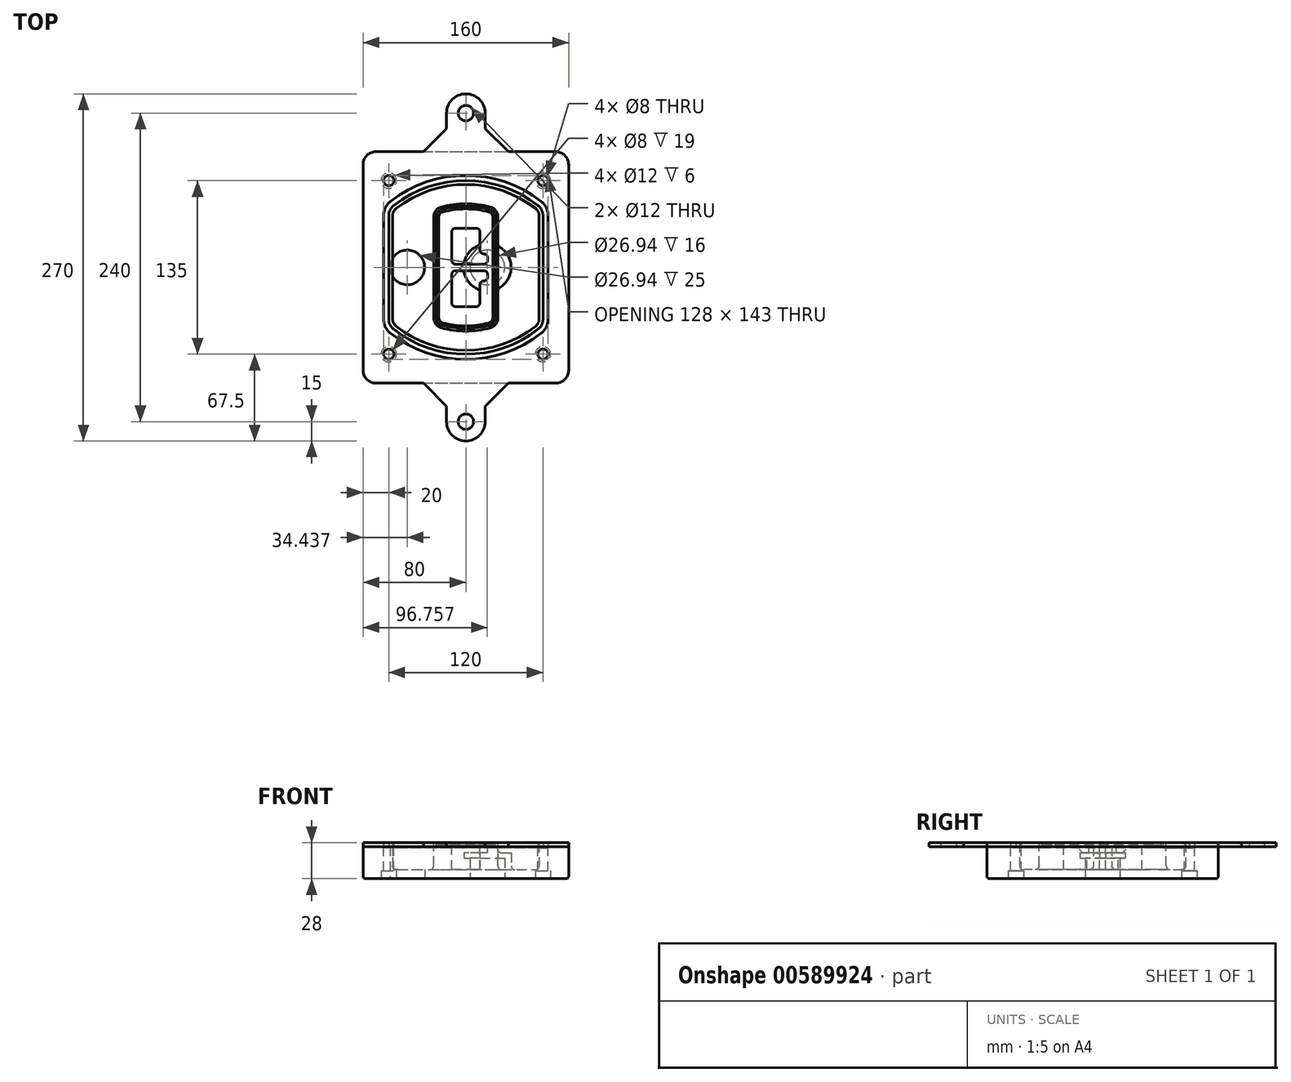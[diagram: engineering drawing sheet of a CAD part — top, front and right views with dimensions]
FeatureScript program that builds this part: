
annotation { "Feature Type Name" : "Feature", "Feature Type Description" : "" }
export const myFeature = defineFeature(function(context is Context, id is Id, definition is map)
    precondition{}
    {
        {
            var Q0;
            Q0=qCreatedBy(makeId("Top.planeOp"),FACE);
            var sketch = newSketch(context, id + "F0", { "sketchPlane" : qUnion([Q0])});
            skPoint(sketch, "E0.rect.middle", {"position": v(0, 0) * mm});
            skLineSegment(sketch, "E1.bottom", {"start": v(-70, -90) * mm, "end": v(70, -90) * mm});
            skLineSegment(sketch, "E1.top", {"start": v(-70, 90) * mm, "end": v(70, 90) * mm});
            skLineSegment(sketch, "E1.left", {"start": v(-80, -80) * mm, "end": v(-80, 80) * mm});
            skLineSegment(sketch, "E1.right", {"start": v(80, -80) * mm, "end": v(80, 80) * mm});
            skLineSegment(sketch, "E2", {"start": v(-80, 90) * mm, "end": v(80, -90) * mm, "construction": true});
            skLineSegment(sketch, "E3", {"start": v(80, 90) * mm, "end": v(-80, -90) * mm, "construction": true});
            skCircle(sketch, "E4", {"center": v(-60, 67.5) * mm, "radius": 4 * mm});
            skCircle(sketch, "E5", {"center": v(60, 67.5) * mm, "radius": 4 * mm});
            skCircle(sketch, "E6", {"center": v(60, -67.5) * mm, "radius": 4 * mm});
            skCircle(sketch, "E7", {"center": v(-60, -67.5) * mm, "radius": 4 * mm});
            skLineSegment(sketch, "E8", {"start": v(-60, 67.5) * mm, "end": v(60, 67.5) * mm, "construction": true});
            skLineSegment(sketch, "E9", {"start": v(60, 67.5) * mm, "end": v(60, -67.5) * mm, "construction": true});
            skLineSegment(sketch, "E10", {"start": v(60, -67.5) * mm, "end": v(-60, -67.5) * mm, "construction": true});
            skLineSegment(sketch, "E11", {"start": v(-60, -67.5) * mm, "end": v(-60, 67.5) * mm, "construction": true});
            skLineSegment(sketch, "E12", {"start": v(-60, 40.3) * mm, "end": v(-60, -40.3) * mm});
            skLineSegment(sketch, "E13", {"start": v(60, 40.3) * mm, "end": v(60, -40.3) * mm});
            skArc(sketch, "E14", {"start": v(56.15, 48.18) * mm, "mid": v(0, 67.5) * mm, "end": v(-56.15, 48.18) * mm});
            skArc(sketch, "E15", {"start": v(-56.15, -48.18) * mm, "mid": v(0, -67.5) * mm, "end": v(56.15, -48.18) * mm});
            skLineSegment(sketch, "E16", {"start": v(-60, 0) * mm, "end": v(60, 0) * mm, "construction": true});
            skPoint(sketch, "E17.visualSharp", {"position": v(-60, -45) * mm});
            skArc(sketch, "E17.filletArc", {"start": v(-60, -40.3) * mm, "mid": v(-58.99, -44.68) * mm, "end": v(-56.15, -48.18) * mm});
            skPoint(sketch, "E18.visualSharp", {"position": v(-60, 45) * mm});
            skArc(sketch, "E18.filletArc", {"start": v(-56.15, 48.18) * mm, "mid": v(-58.99, 44.68) * mm, "end": v(-60, 40.3) * mm});
            skPoint(sketch, "E19.visualSharp", {"position": v(60, 45) * mm});
            skArc(sketch, "E19.filletArc", {"start": v(60, 40.3) * mm, "mid": v(58.99, 44.68) * mm, "end": v(56.15, 48.18) * mm});
            skPoint(sketch, "E20.visualSharp", {"position": v(60, -45) * mm});
            skArc(sketch, "E20.filletArc", {"start": v(56.15, -48.18) * mm, "mid": v(58.99, -44.68) * mm, "end": v(60, -40.3) * mm});
            skPoint(sketch, "E21.visualSharp", {"position": v(-80, 90) * mm});
            skArc(sketch, "E21.filletArc", {"start": v(-70, 90) * mm, "mid": v(-77.07, 87.07) * mm, "end": v(-80, 80) * mm});
            skPoint(sketch, "E22.visualSharp", {"position": v(80, 90) * mm});
            skArc(sketch, "E22.filletArc", {"start": v(80, 80) * mm, "mid": v(77.07, 87.07) * mm, "end": v(70, 90) * mm});
            skPoint(sketch, "E23.visualSharp", {"position": v(80, -90) * mm});
            skArc(sketch, "E23.filletArc", {"start": v(70, -90) * mm, "mid": v(77.07, -87.07) * mm, "end": v(80, -80) * mm});
            skPoint(sketch, "E24.visualSharp", {"position": v(-80, -90) * mm});
            skArc(sketch, "E24.filletArc", {"start": v(-80, -80) * mm, "mid": v(-77.07, -87.07) * mm, "end": v(-70, -90) * mm});
            skArc(sketch, "E25.0", {"start": v(57, 40.3) * mm, "mid": v(56.3, 43.36) * mm, "end": v(54.3, 45.81) * mm});
            skLineSegment(sketch, "E25.1", {"start": v(57, 40.3) * mm, "end": v(57, -40.3) * mm});
            skArc(sketch, "E25.2", {"start": v(54.3, -45.81) * mm, "mid": v(56.3, -43.36) * mm, "end": v(57, -40.3) * mm});
            skArc(sketch, "E25.3", {"start": v(-54.3, -45.81) * mm, "mid": v(0, -64.5) * mm, "end": v(54.3, -45.81) * mm});
            skArc(sketch, "E25.4", {"start": v(-57, -40.3) * mm, "mid": v(-56.3, -43.36) * mm, "end": v(-54.3, -45.81) * mm});
            skArc(sketch, "E25.5", {"start": v(54.3, 45.81) * mm, "mid": v(0, 64.5) * mm, "end": v(-54.3, 45.81) * mm});
            skLineSegment(sketch, "E25.6", {"start": v(-57, 40.3) * mm, "end": v(-57, -40.3) * mm});
            skArc(sketch, "E25.7", {"start": v(-54.3, 45.81) * mm, "mid": v(-56.3, 43.36) * mm, "end": v(-57, 40.3) * mm});
            skArc(sketch, "E26.0", {"start": v(-58.62, 51.33) * mm, "mid": v(-62.58, 46.43) * mm, "end": v(-64, 40.3) * mm});
            skArc(sketch, "E26.1", {"start": v(58.62, 51.33) * mm, "mid": v(0, 71.5) * mm, "end": v(-58.62, 51.33) * mm});
            skArc(sketch, "E26.2", {"start": v(64, 40.3) * mm, "mid": v(62.58, 46.43) * mm, "end": v(58.62, 51.33) * mm});
            skLineSegment(sketch, "E26.3", {"start": v(64, 40.3) * mm, "end": v(64, -40.3) * mm});
            skArc(sketch, "E26.4", {"start": v(58.62, -51.33) * mm, "mid": v(62.58, -46.43) * mm, "end": v(64, -40.3) * mm});
            skLineSegment(sketch, "E26.5", {"start": v(-64, 40.3) * mm, "end": v(-64, -40.3) * mm});
            skArc(sketch, "E26.6", {"start": v(-58.62, -51.33) * mm, "mid": v(0, -71.5) * mm, "end": v(58.62, -51.33) * mm});
            skArc(sketch, "E26.7", {"start": v(-64, -40.3) * mm, "mid": v(-62.58, -46.43) * mm, "end": v(-58.62, -51.33) * mm});
            skLineSegment(sketch, "E27", {"start": v(0, 90) * mm, "end": v(0, 120) * mm, "construction": true});
            skCircle(sketch, "E28", {"center": v(0, 120) * mm, "radius": 6 * mm});
            skArc(sketch, "E29", {"start": v(15, 120) * mm, "mid": v(0, 135) * mm, "end": v(-15, 120) * mm});
            skLineSegment(sketch, "E30", {"start": v(-15, 120) * mm, "end": v(-15, 108) * mm});
            skLineSegment(sketch, "E31", {"start": v(15, 120) * mm, "end": v(15, 108) * mm});
            skLineSegment(sketch, "E32", {"start": v(-15, 108) * mm, "end": v(-33, 90) * mm});
            skLineSegment(sketch, "E33", {"start": v(15, 108) * mm, "end": v(33, 90) * mm});
            skLineSegment(sketch, "E34.MirrorCS", {"start": v(-15, -108) * mm, "end": v(-33, -90) * mm});
            skLineSegment(sketch, "E35.MirrorCS", {"start": v(-15, -120) * mm, "end": v(-15, -108) * mm});
            skArc(sketch, "E36.MirrorCS", {"start": v(15, -120) * mm, "mid": v(0, -135) * mm, "end": v(-15, -120) * mm});
            skCircle(sketch, "E37.MirrorC", {"center": v(0, -120) * mm, "radius": 6 * mm});
            skLineSegment(sketch, "E38.MirrorCS", {"start": v(15, -120) * mm, "end": v(15, -108) * mm});
            skLineSegment(sketch, "E39.MirrorCS", {"start": v(15, -108) * mm, "end": v(33, -90) * mm});
            skLineSegment(sketch, "E40.MirrorCS", {"start": v(0, -90) * mm, "end": v(0, -120) * mm, "construction": true});
            skSolve(sketch);
        }
        {
            var Q0;
            Q0=makeQuery(id+"F0.imprint","IMPRINT",FACE,{"disambiguationData":[TD([[makeQuery(id+"F0.imprint","IMPRINT",EDGE,{"derivedFrom":sQuery(id+"F0.wireOp",EDGE,"E1.bottom")}),1.0]])]});
            var Q1;
            Q1=makeQuery(id+"F0.imprint","IMPRINT",FACE,{"disambiguationData":[TD([[makeQuery(id+"F0.imprint","IMPRINT",EDGE,{"derivedFrom":sQuery(id+"F0.wireOp",EDGE,"E12")}),1.0]])]});
            var Q2;
            Q2=makeQuery(id+"F0.imprint","IMPRINT",FACE,{"disambiguationData":[TD([[makeQuery(id+"F0.imprint","IMPRINT",EDGE,{"derivedFrom":sQuery(id+"F0.wireOp",EDGE,"E25.0")}),1.0]])]});
            var Q3;
            Q3=makeQuery(id+"F0.imprint","IMPRINT",FACE,{"disambiguationData":[TD([[makeQuery(id+"F0.imprint","IMPRINT",EDGE,{"derivedFrom":sQuery(id+"F0.wireOp",EDGE,"E12")}),-1.0]])]});
            extrude(context, id + "F1", {"entities" : qUnion([Q0, Q1, Q2, Q3]), "oppositeDirection" : true, "depth" : 25 * mm});
        }
        {
            var Q0;
            Q0=makeQuery(id+"F0.imprint","IMPRINT",FACE,{"disambiguationData":[TD([[makeQuery(id+"F0.imprint","IMPRINT",EDGE,{"derivedFrom":sQuery(id+"F0.wireOp",EDGE,"E12")}),1.0]])]});
            extrude(context, id + "F2", {"entities" : qUnion([Q0]), "operationType" : NewBodyOperationType.ADD, "depth" : 3 * mm});
        }
        {
            var Q0;
            Q0=makeQuery(id+"F0.imprint","IMPRINT",FACE,{"disambiguationData":[TD([[makeQuery(id+"F0.imprint","IMPRINT",EDGE,{"derivedFrom":sQuery(id+"F0.wireOp",EDGE,"E12")}),-1.0]])]});
            extrude(context, id + "F3", {"entities" : qUnion([Q0]), "operationType" : NewBodyOperationType.REMOVE, "oppositeDirection" : true, "depth" : 1 * mm});
        }
        {
            var Q0;
            Q0=makeQuery(id+"F0.imprint","IMPRINT",FACE,{"disambiguationData":[TD([[makeQuery(id+"F0.imprint","IMPRINT",EDGE,{"derivedFrom":sQuery(id+"F0.wireOp",EDGE,"E25.0")}),1.0]])]});
            extrude(context, id + "F4", {"entities" : qUnion([Q0]), "operationType" : NewBodyOperationType.REMOVE, "oppositeDirection" : true, "depth" : 18 * mm});
        }
        {
            var Q0;
            Q0=makeQuery(id+"F2.opExtrude","CAP_FACE",FACE,{"disambiguationData":[OSD([sQuery(id+"F0.wireOp",EDGE,"E12"),sQuery(id+"F0.wireOp",EDGE,"E13"),sQuery(id+"F0.wireOp",EDGE,"E14"),sQuery(id+"F0.wireOp",EDGE,"E15"),sQuery(id+"F0.wireOp",EDGE,"E17.filletArc"),sQuery(id+"F0.wireOp",EDGE,"E18.filletArc"),sQuery(id+"F0.wireOp",EDGE,"E19.filletArc"),sQuery(id+"F0.wireOp",EDGE,"E20.filletArc"),sQuery(id+"F0.wireOp",EDGE,"E25.0"),sQuery(id+"F0.wireOp",EDGE,"E25.1"),sQuery(id+"F0.wireOp",EDGE,"E25.2"),sQuery(id+"F0.wireOp",EDGE,"E25.3"),sQuery(id+"F0.wireOp",EDGE,"E25.4"),sQuery(id+"F0.wireOp",EDGE,"E25.5"),sQuery(id+"F0.wireOp",EDGE,"E25.6"),sQuery(id+"F0.wireOp",EDGE,"E25.7")])],"isStart":false});
            var sketch = newSketch(context, id + "F5", { "sketchPlane" : qUnion([Q0])});
            skArc(sketch, "E41.0", {"start": v(-19.08, -46.97) * mm, "mid": v(0, -49.5) * mm, "end": v(19.08, -46.97) * mm});
            skArc(sketch, "E42.0", {"start": v(19.08, 46.97) * mm, "mid": v(0, 49.5) * mm, "end": v(-19.08, 46.97) * mm});
            skLineSegment(sketch, "E43", {"start": v(-25, 39.25) * mm, "end": v(-25, -39.25) * mm});
            skLineSegment(sketch, "E44", {"start": v(25, 39.25) * mm, "end": v(25, -39.25) * mm});
            skLineSegment(sketch, "E45", {"start": v(-25, 45.1) * mm, "end": v(25, 45.1) * mm, "construction": true});
            skLineSegment(sketch, "E46", {"start": v(-25, -45.1) * mm, "end": v(25, -45.1) * mm, "construction": true});
            skPoint(sketch, "E47.visualSharp", {"position": v(-25, 45.1) * mm});
            skArc(sketch, "E47.filletArc", {"start": v(-19.08, 46.97) * mm, "mid": v(-23.35, 44.11) * mm, "end": v(-25, 39.25) * mm});
            skPoint(sketch, "E48.visualSharp", {"position": v(25, 45.1) * mm});
            skArc(sketch, "E48.filletArc", {"start": v(25, 39.25) * mm, "mid": v(23.35, 44.11) * mm, "end": v(19.08, 46.97) * mm});
            skPoint(sketch, "E49.visualSharp", {"position": v(25, -45.1) * mm});
            skArc(sketch, "E49.filletArc", {"start": v(19.08, -46.97) * mm, "mid": v(23.35, -44.11) * mm, "end": v(25, -39.25) * mm});
            skPoint(sketch, "E50.visualSharp", {"position": v(-25, -45.1) * mm});
            skArc(sketch, "E50.filletArc", {"start": v(-25, -39.25) * mm, "mid": v(-23.35, -44.11) * mm, "end": v(-19.08, -46.97) * mm});
            skArc(sketch, "E51.0", {"start": v(54.3, 45.81) * mm, "mid": v(0, 64.5) * mm, "end": v(-54.3, 45.81) * mm});
            skArc(sketch, "E51.1", {"start": v(-54.3, 45.81) * mm, "mid": v(-56.3, 43.36) * mm, "end": v(-57, 40.3) * mm});
            skLineSegment(sketch, "E51.2", {"start": v(-57, 40.3) * mm, "end": v(-57, -40.3) * mm});
            skArc(sketch, "E51.3", {"start": v(-57, -40.3) * mm, "mid": v(-56.3, -43.36) * mm, "end": v(-54.3, -45.81) * mm});
            skArc(sketch, "E51.4", {"start": v(-54.3, -45.81) * mm, "mid": v(0, -64.5) * mm, "end": v(54.3, -45.81) * mm});
            skArc(sketch, "E51.5", {"start": v(54.3, -45.81) * mm, "mid": v(56.3, -43.36) * mm, "end": v(57, -40.3) * mm});
            skLineSegment(sketch, "E51.6", {"start": v(57, 40.3) * mm, "end": v(57, -40.3) * mm});
            skArc(sketch, "E51.7", {"start": v(57, 40.3) * mm, "mid": v(56.3, 43.36) * mm, "end": v(54.3, 45.81) * mm});
            skLineSegment(sketch, "E52.0", {"start": v(23, 39.25) * mm, "end": v(23, -39.25) * mm});
            skArc(sketch, "E52.1", {"start": v(18.56, -45.04) * mm, "mid": v(21.76, -42.9) * mm, "end": v(23, -39.25) * mm});
            skArc(sketch, "E52.2", {"start": v(-18.56, -45.04) * mm, "mid": v(0, -47.5) * mm, "end": v(18.56, -45.04) * mm});
            skArc(sketch, "E52.3", {"start": v(-23, -39.25) * mm, "mid": v(-21.76, -42.9) * mm, "end": v(-18.56, -45.04) * mm});
            skLineSegment(sketch, "E52.4", {"start": v(-23, 39.25) * mm, "end": v(-23, -39.25) * mm});
            skArc(sketch, "E52.5", {"start": v(23, 39.25) * mm, "mid": v(21.76, 42.9) * mm, "end": v(18.56, 45.04) * mm});
            skArc(sketch, "E52.6", {"start": v(-18.56, 45.04) * mm, "mid": v(-21.76, 42.9) * mm, "end": v(-23, 39.25) * mm});
            skArc(sketch, "E52.7", {"start": v(18.56, 45.04) * mm, "mid": v(0, 47.5) * mm, "end": v(-18.56, 45.04) * mm});
            skArc(sketch, "E53.0", {"start": v(21, 39.25) * mm, "mid": v(20.18, 41.68) * mm, "end": v(18.04, 43.1) * mm});
            skLineSegment(sketch, "E53.1", {"start": v(21, 39.25) * mm, "end": v(21, -39.25) * mm});
            skArc(sketch, "E53.2", {"start": v(18.04, -43.1) * mm, "mid": v(20.18, -41.68) * mm, "end": v(21, -39.25) * mm});
            skArc(sketch, "E53.3", {"start": v(-18.04, -43.1) * mm, "mid": v(0, -45.5) * mm, "end": v(18.04, -43.1) * mm});
            skArc(sketch, "E53.4", {"start": v(-21, -39.25) * mm, "mid": v(-20.18, -41.68) * mm, "end": v(-18.04, -43.1) * mm});
            skArc(sketch, "E53.5", {"start": v(18.04, 43.1) * mm, "mid": v(0, 45.5) * mm, "end": v(-18.04, 43.1) * mm});
            skLineSegment(sketch, "E53.6", {"start": v(-21, 39.25) * mm, "end": v(-21, -39.25) * mm});
            skArc(sketch, "E53.7", {"start": v(-18.04, 43.1) * mm, "mid": v(-20.18, 41.68) * mm, "end": v(-21, 39.25) * mm});
            skLineSegment(sketch, "E54", {"start": v(-25, 0) * mm, "end": v(25, 0) * mm, "construction": true});
            skLineSegment(sketch, "E55", {"start": v(-11, 5.5) * mm, "end": v(-11, 27.5) * mm});
            skLineSegment(sketch, "E56", {"start": v(-8, 30.5) * mm, "end": v(8, 30.5) * mm});
            skLineSegment(sketch, "E57", {"start": v(11, 27.5) * mm, "end": v(11, 13.5) * mm});
            skLineSegment(sketch, "E58", {"start": v(14, 10.5) * mm, "end": v(14, 10.5) * mm});
            skLineSegment(sketch, "E59", {"start": v(17, 7.5) * mm, "end": v(17, 5.5) * mm});
            skLineSegment(sketch, "E60", {"start": v(14, 2.5) * mm, "end": v(-8, 2.5) * mm});
            skPoint(sketch, "E61.visualSharp", {"position": v(-11, 30.5) * mm});
            skArc(sketch, "E61.filletArc", {"start": v(-8, 30.5) * mm, "mid": v(-10.12, 29.62) * mm, "end": v(-11, 27.5) * mm});
            skPoint(sketch, "E62.visualSharp", {"position": v(11, 30.5) * mm});
            skArc(sketch, "E62.filletArc", {"start": v(11, 27.5) * mm, "mid": v(10.12, 29.62) * mm, "end": v(8, 30.5) * mm});
            skPoint(sketch, "E63.visualSharp", {"position": v(11, 10.5) * mm});
            skArc(sketch, "E63.filletArc", {"start": v(11, 13.5) * mm, "mid": v(11.88, 11.38) * mm, "end": v(14, 10.5) * mm});
            skPoint(sketch, "E64.visualSharp", {"position": v(17, 10.5) * mm});
            skArc(sketch, "E64.filletArc", {"start": v(17, 7.5) * mm, "mid": v(16.12, 9.62) * mm, "end": v(14, 10.5) * mm});
            skPoint(sketch, "E65.visualSharp", {"position": v(17, 2.5) * mm});
            skArc(sketch, "E65.filletArc", {"start": v(14, 2.5) * mm, "mid": v(16.12, 3.38) * mm, "end": v(17, 5.5) * mm});
            skPoint(sketch, "E66.visualSharp", {"position": v(-11, 2.5) * mm});
            skArc(sketch, "E66.filletArc", {"start": v(-11, 5.5) * mm, "mid": v(-10.12, 3.38) * mm, "end": v(-8, 2.5) * mm});
            skLineSegment(sketch, "E67.0.MirrorCS", {"start": v(14, -2.5) * mm, "end": v(-8, -2.5) * mm});
            skArc(sketch, "E68.0.MirrorCS", {"start": v(-11, -5.5) * mm, "mid": v(-10.12, -3.38) * mm, "end": v(-8, -2.5) * mm});
            skLineSegment(sketch, "E69.0.MirrorCS", {"start": v(-11, -5.5) * mm, "end": v(-11, -27.5) * mm});
            skArc(sketch, "E70.0.MirrorCS", {"start": v(-8, -30.5) * mm, "mid": v(-10.12, -29.62) * mm, "end": v(-11, -27.5) * mm});
            skLineSegment(sketch, "E71.0.MirrorCS", {"start": v(-8, -30.5) * mm, "end": v(8, -30.5) * mm});
            skArc(sketch, "E72.0.MirrorCS", {"start": v(11, -27.5) * mm, "mid": v(10.12, -29.62) * mm, "end": v(8, -30.5) * mm});
            skLineSegment(sketch, "E73.0.MirrorCS", {"start": v(11, -27.5) * mm, "end": v(11, -13.5) * mm});
            skArc(sketch, "E74.0.MirrorCS", {"start": v(11, -13.5) * mm, "mid": v(11.88, -11.38) * mm, "end": v(14, -10.5) * mm});
            skArc(sketch, "E75.0.MirrorCS", {"start": v(17, -7.5) * mm, "mid": v(16.12, -9.62) * mm, "end": v(14, -10.5) * mm});
            skLineSegment(sketch, "E76.0.MirrorCS", {"start": v(17, -7.5) * mm, "end": v(17, -5.5) * mm});
            skArc(sketch, "E77.0.MirrorCS", {"start": v(14, -2.5) * mm, "mid": v(16.12, -3.38) * mm, "end": v(17, -5.5) * mm});
            skSolve(sketch);
        }
        {
            var Q0;
            Q0=makeQuery(id+"F5.imprint","IMPRINT",FACE,{"disambiguationData":[TD([[makeQuery(id+"F5.imprint","IMPRINT",EDGE,{"derivedFrom":sQuery(id+"F5.wireOp",EDGE,"E41.0")}),1.0]])]});
            var Q1;
            Q1=makeQuery(id+"F5.imprint","IMPRINT",FACE,{"disambiguationData":[TD([[makeQuery(id+"F5.imprint","IMPRINT",EDGE,{"derivedFrom":sQuery(id+"F5.wireOp",EDGE,"E52.0")}),-1.0]])]});
            var Q2;
            Q2=makeQuery(id+"F5.imprint","IMPRINT",FACE,{"disambiguationData":[TD([[makeQuery(id+"F5.imprint","IMPRINT",EDGE,{"derivedFrom":sQuery(id+"F5.wireOp",EDGE,"E53.0")}),1.0]])]});
            extrude(context, id + "F6", {"entities" : qUnion([Q0, Q1, Q2]), "operationType" : NewBodyOperationType.ADD, "endBound" : BoundingType.UP_TO_NEXT, "oppositeDirection" : true, "depth" : 25 * mm});
        }
        {
            var Q0;
            Q0=makeQuery(id+"F5.imprint","IMPRINT",FACE,{"disambiguationData":[TD([[makeQuery(id+"F5.imprint","IMPRINT",EDGE,{"derivedFrom":sQuery(id+"F5.wireOp",EDGE,"E52.0")}),-1.0]])]});
            extrude(context, id + "F7", {"entities" : qUnion([Q0]), "operationType" : NewBodyOperationType.REMOVE, "oppositeDirection" : true, "depth" : 2 * mm});
        }
        {
            var Q0;
            Q0=makeQuery(id+"F1.opExtrude","CAP_FACE",FACE,{"disambiguationData":[OSD([sQuery(id+"F0.wireOp",EDGE,"E1.bottom"),sQuery(id+"F0.wireOp",EDGE,"E1.top"),sQuery(id+"F0.wireOp",EDGE,"E1.left"),sQuery(id+"F0.wireOp",EDGE,"E1.right"),sQuery(id+"F0.wireOp",EDGE,"E4"),sQuery(id+"F0.wireOp",EDGE,"E5"),sQuery(id+"F0.wireOp",EDGE,"E6"),sQuery(id+"F0.wireOp",EDGE,"E7"),sQuery(id+"F0.wireOp",EDGE,"E21.filletArc"),sQuery(id+"F0.wireOp",EDGE,"E22.filletArc"),sQuery(id+"F0.wireOp",EDGE,"E23.filletArc"),sQuery(id+"F0.wireOp",EDGE,"E24.filletArc")])],"isStart":false});
            var sketch = newSketch(context, id + "F8", { "sketchPlane" : qUnion([Q0])});
            skCircle(sketch, "E78", {"center": v(16.76, 0) * mm, "radius": 13.47 * mm});
            skCircle(sketch, "E79", {"center": v(-45.56, 0) * mm, "radius": 13.47 * mm});
            skLineSegment(sketch, "E80", {"start": v(80, 0) * mm, "end": v(-80, 0) * mm});
            skCircle(sketch, "E81", {"center": v(16.76, 0) * mm, "radius": 18.47 * mm});
            skCircle(sketch, "E82", {"center": v(60, -67.5) * mm, "radius": 6 * mm});
            skCircle(sketch, "E83", {"center": v(-60, -67.5) * mm, "radius": 6 * mm});
            skCircle(sketch, "E84", {"center": v(-60, 67.5) * mm, "radius": 6 * mm});
            skCircle(sketch, "E85", {"center": v(60, 67.5) * mm, "radius": 6 * mm});
            skSolve(sketch);
        }
        {
            var Q0;
            {var subQ1=sQuery(id+"F8.wireOp",EDGE,"E80");var subQ4=sQuery(id+"F8.wireOp",EDGE,"E78");var subQ6=makeQuery(id+"F8.imprint","INTERSECT",VERTEX,{"disambiguationData":[OD(0.0)],"derivedFrom":[subQ4,subQ1]});Q0=makeQuery(id+"F8.imprint","IMPRINT",FACE,{"disambiguationData":[TD([[makeQuery(id+"F8.imprint","IMPRINT",EDGE,{"disambiguationData":[TD([[subQ6,-1.0]])],"derivedFrom":subQ4}),-1.0]])]});}
            var Q1;
            {var subQ0=sQuery(id+"F8.wireOp",EDGE,"E80");var subQ1=sQuery(id+"F8.wireOp",EDGE,"E78");var subQ3=makeQuery(id+"F8.imprint","INTERSECT",VERTEX,{"disambiguationData":[OD(0.0)],"derivedFrom":[subQ1,subQ0]});Q1=makeQuery(id+"F8.imprint","IMPRINT",FACE,{"disambiguationData":[TD([[makeQuery(id+"F8.imprint","IMPRINT",EDGE,{"disambiguationData":[TD([[subQ3,-1.0]])],"derivedFrom":subQ1}),1.0]])]});}
            var Q2;
            {var subQ0=sQuery(id+"F8.wireOp",EDGE,"E80");var subQ1=sQuery(id+"F8.wireOp",EDGE,"E78");var subQ3=makeQuery(id+"F8.imprint","INTERSECT",VERTEX,{"disambiguationData":[OD(0.0)],"derivedFrom":[subQ1,subQ0]});Q2=makeQuery(id+"F8.imprint","IMPRINT",FACE,{"disambiguationData":[TD([[makeQuery(id+"F8.imprint","IMPRINT",EDGE,{"disambiguationData":[TD([[subQ3,1.0]])],"derivedFrom":subQ1}),1.0]])]});}
            var Q3;
            {var subQ1=sQuery(id+"F8.wireOp",EDGE,"E80");var subQ4=sQuery(id+"F8.wireOp",EDGE,"E78");var subQ6=makeQuery(id+"F8.imprint","INTERSECT",VERTEX,{"disambiguationData":[OD(0.0)],"derivedFrom":[subQ4,subQ1]});Q3=makeQuery(id+"F8.imprint","IMPRINT",FACE,{"disambiguationData":[TD([[makeQuery(id+"F8.imprint","IMPRINT",EDGE,{"disambiguationData":[TD([[subQ6,1.0]])],"derivedFrom":subQ4}),-1.0]])]});}
            extrude(context, id + "F9", {"entities" : qUnion([Q0, Q1, Q2, Q3]), "operationType" : NewBodyOperationType.ADD, "oppositeDirection" : true, "depth" : 20 * mm});
        }
        {
            var Q0;
            {var subQ0=sQuery(id+"F8.wireOp",EDGE,"E80");var subQ1=sQuery(id+"F8.wireOp",EDGE,"E78");var subQ3=makeQuery(id+"F8.imprint","INTERSECT",VERTEX,{"disambiguationData":[OD(0.0)],"derivedFrom":[subQ1,subQ0]});Q0=makeQuery(id+"F8.imprint","IMPRINT",FACE,{"disambiguationData":[TD([[makeQuery(id+"F8.imprint","IMPRINT",EDGE,{"disambiguationData":[TD([[subQ3,-1.0]])],"derivedFrom":subQ1}),1.0]])]});}
            var Q1;
            {var subQ0=sQuery(id+"F8.wireOp",EDGE,"E80");var subQ1=sQuery(id+"F8.wireOp",EDGE,"E78");var subQ3=makeQuery(id+"F8.imprint","INTERSECT",VERTEX,{"disambiguationData":[OD(0.0)],"derivedFrom":[subQ1,subQ0]});Q1=makeQuery(id+"F8.imprint","IMPRINT",FACE,{"disambiguationData":[TD([[makeQuery(id+"F8.imprint","IMPRINT",EDGE,{"disambiguationData":[TD([[subQ3,1.0]])],"derivedFrom":subQ1}),1.0]])]});}
            extrude(context, id + "F10", {"entities" : qUnion([Q0, Q1]), "operationType" : NewBodyOperationType.REMOVE, "oppositeDirection" : true, "depth" : 16 * mm});
        }
        {
            var Q0;
            {var subQ0=sQuery(id+"F8.wireOp",EDGE,"E80");var subQ1=sQuery(id+"F8.wireOp",EDGE,"E79");var subQ3=makeQuery(id+"F8.imprint","INTERSECT",VERTEX,{"disambiguationData":[OD(0.0)],"derivedFrom":[subQ1,subQ0]});Q0=makeQuery(id+"F8.imprint","IMPRINT",FACE,{"disambiguationData":[TD([[makeQuery(id+"F8.imprint","IMPRINT",EDGE,{"disambiguationData":[TD([[subQ3,-1.0]])],"derivedFrom":subQ1}),1.0]])]});}
            var Q1;
            {var subQ0=sQuery(id+"F8.wireOp",EDGE,"E80");var subQ1=sQuery(id+"F8.wireOp",EDGE,"E79");var subQ3=makeQuery(id+"F8.imprint","INTERSECT",VERTEX,{"disambiguationData":[OD(0.0)],"derivedFrom":[subQ1,subQ0]});Q1=makeQuery(id+"F8.imprint","IMPRINT",FACE,{"disambiguationData":[TD([[makeQuery(id+"F8.imprint","IMPRINT",EDGE,{"disambiguationData":[TD([[subQ3,1.0]])],"derivedFrom":subQ1}),1.0]])]});}
            extrude(context, id + "F11", {"entities" : qUnion([Q0, Q1]), "operationType" : NewBodyOperationType.REMOVE, "oppositeDirection" : true, "depth" : 25 * mm});
        }
        {
            var Q0;
            Q0=makeQuery(id+"F8.imprint","IMPRINT",FACE,{"disambiguationData":[TD([[makeQuery(id+"F8.imprint","IMPRINT",EDGE,{"derivedFrom":sQuery(id+"F8.wireOp",EDGE,"E82")}),1.0]])]});
            var Q1;
            Q1=makeQuery(id+"F8.imprint","IMPRINT",FACE,{"disambiguationData":[TD([[makeQuery(id+"F8.imprint","IMPRINT",EDGE,{"derivedFrom":makeQuery(id+"F1.opExtrude","CAP_EDGE",EDGE,{"disambiguationData":[OSD([sQuery(id+"F0.wireOp",EDGE,"E5")])],"isStart":false})}),-1.0]])]});
            var Q2;
            Q2=makeQuery(id+"F8.imprint","IMPRINT",FACE,{"disambiguationData":[TD([[makeQuery(id+"F8.imprint","IMPRINT",EDGE,{"derivedFrom":sQuery(id+"F8.wireOp",EDGE,"E83")}),1.0]])]});
            var Q3;
            Q3=makeQuery(id+"F8.imprint","IMPRINT",FACE,{"disambiguationData":[TD([[makeQuery(id+"F8.imprint","IMPRINT",EDGE,{"derivedFrom":makeQuery(id+"F1.opExtrude","CAP_EDGE",EDGE,{"disambiguationData":[OSD([sQuery(id+"F0.wireOp",EDGE,"E4")])],"isStart":false})}),-1.0]])]});
            var Q4;
            Q4=makeQuery(id+"F8.imprint","IMPRINT",FACE,{"disambiguationData":[TD([[makeQuery(id+"F8.imprint","IMPRINT",EDGE,{"derivedFrom":sQuery(id+"F8.wireOp",EDGE,"E84")}),1.0]])]});
            var Q5;
            Q5=makeQuery(id+"F8.imprint","IMPRINT",FACE,{"disambiguationData":[TD([[makeQuery(id+"F8.imprint","IMPRINT",EDGE,{"derivedFrom":makeQuery(id+"F1.opExtrude","CAP_EDGE",EDGE,{"disambiguationData":[OSD([sQuery(id+"F0.wireOp",EDGE,"E7")])],"isStart":false})}),-1.0]])]});
            var Q6;
            Q6=makeQuery(id+"F8.imprint","IMPRINT",FACE,{"disambiguationData":[TD([[makeQuery(id+"F8.imprint","IMPRINT",EDGE,{"derivedFrom":sQuery(id+"F8.wireOp",EDGE,"E85")}),1.0]])]});
            var Q7;
            Q7=makeQuery(id+"F8.imprint","IMPRINT",FACE,{"disambiguationData":[TD([[makeQuery(id+"F8.imprint","IMPRINT",EDGE,{"derivedFrom":makeQuery(id+"F1.opExtrude","CAP_EDGE",EDGE,{"disambiguationData":[OSD([sQuery(id+"F0.wireOp",EDGE,"E6")])],"isStart":false})}),-1.0]])]});
            extrude(context, id + "F12", {"entities" : qUnion([Q0, Q1, Q2, Q3, Q4, Q5, Q6, Q7]), "operationType" : NewBodyOperationType.REMOVE, "oppositeDirection" : true, "depth" : 6 * mm});
        }
        {
            var Q0;
            Q0=makeQuery(id+"F10.boolean.opBoolean","COPY",FACE,{"derivedFrom":makeQuery(id+"F10.opExtrude","CAP_FACE",FACE,{"disambiguationData":[OSD([sQuery(id+"F8.wireOp",EDGE,"E78")])],"isStart":false})});
            var sketch = newSketch(context, id + "F13", { "sketchPlane" : qUnion([Q0])});
            skArc(sketch, "E86.0", {"start": v(11, 17.55) * mm, "mid": v(2.57, 11.82) * mm, "end": v(-1.54, 2.5) * mm});
            skArc(sketch, "E86.1", {"start": v(-1.54, -2.5) * mm, "mid": v(2.57, -11.82) * mm, "end": v(11, -17.55) * mm});
            skLineSegment(sketch, "E87", {"start": v(-1.54, -2.5) * mm, "end": v(14, -2.5) * mm});
            skLineSegment(sketch, "E88.0", {"start": v(14, 2.5) * mm, "end": v(-1.54, 2.5) * mm});
            skArc(sketch, "E88.1", {"start": v(14, 2.5) * mm, "mid": v(16.12, 3.38) * mm, "end": v(17, 5.5) * mm});
            skLineSegment(sketch, "E88.2", {"start": v(17, 7.5) * mm, "end": v(17, 5.5) * mm});
            skArc(sketch, "E88.3", {"start": v(17, 7.5) * mm, "mid": v(16.12, 9.62) * mm, "end": v(14, 10.5) * mm});
            skArc(sketch, "E88.4", {"start": v(11, 13.5) * mm, "mid": v(11.88, 11.38) * mm, "end": v(14, 10.5) * mm});
            skLineSegment(sketch, "E88.5", {"start": v(11, 17.55) * mm, "end": v(11, 13.5) * mm});
            skLineSegment(sketch, "E88.7", {"start": v(14, -2.5) * mm, "end": v(-1.54, -2.5) * mm});
            skArc(sketch, "E88.8", {"start": v(14, -2.5) * mm, "mid": v(16.12, -3.38) * mm, "end": v(17, -5.5) * mm});
            skLineSegment(sketch, "E88.9", {"start": v(17, -7.5) * mm, "end": v(17, -5.5) * mm});
            skArc(sketch, "E88.10", {"start": v(17, -7.5) * mm, "mid": v(16.12, -9.62) * mm, "end": v(14, -10.5) * mm});
            skArc(sketch, "E88.11", {"start": v(11, -13.5) * mm, "mid": v(11.88, -11.38) * mm, "end": v(14, -10.5) * mm});
            skLineSegment(sketch, "E88.12", {"start": v(11, -17.55) * mm, "end": v(11, -13.5) * mm});
            skPoint(sketch, "E89.orphan", {"position": v(11, -27.5) * mm});
            skPoint(sketch, "E90.orphan", {"position": v(-8, -2.5) * mm});
            skPoint(sketch, "E91.orphan", {"position": v(-8, 2.5) * mm});
            skPoint(sketch, "E92.orphan", {"position": v(11, 27.5) * mm});
            skSolve(sketch);
        }
        {
            var Q0;
            {var subQ7=sQuery(id+"F13.wireOp",EDGE,"E86.0");var subQ14=sQuery(id+"F13.wireOp",EDGE,"E86.1");var subQ16=sQuery(id+"F13.wireOp",EDGE,"E88.1");var subQ18=sQuery(id+"F13.wireOp",EDGE,"E88.8");Q0=qUnion([makeQuery(id+"F13.imprint","IMPRINT",FACE,{"disambiguationData":[TD([[makeQuery(id+"F13.imprint","IMPRINT",EDGE,{"derivedFrom":subQ7}),1.0]])]}),makeQuery(id+"F13.imprint","IMPRINT",FACE,{"disambiguationData":[TD([[makeQuery(id+"F13.imprint","IMPRINT",EDGE,{"derivedFrom":subQ14}),1.0]])]}),makeQuery(id+"F13.imprint","IMPRINT",FACE,{"disambiguationData":[TD([[makeQuery(id+"F13.imprint","IMPRINT",EDGE,{"derivedFrom":subQ16}),1.0]])]}),makeQuery(id+"F13.imprint","IMPRINT",FACE,{"disambiguationData":[TD([[makeQuery(id+"F13.imprint","IMPRINT",EDGE,{"derivedFrom":subQ18}),-1.0]])]})]);}
            var Q1;
            Q1=makeQuery(id+"F6.boolean.opBoolean","SPLIT",FACE,{"disambiguationData":[TD([makeQuery(id+"F6.opExtrude","SWEPT_FACE",FACE,{"disambiguationData":[OSD([sQuery(id+"F5.wireOp",EDGE,"E55")])]})])],"derivedFrom":makeQuery(id+"F4.boolean.opBoolean","COPY",FACE,{"derivedFrom":makeQuery(id+"F4.opExtrude","CAP_FACE",FACE,{"disambiguationData":[OSD([sQuery(id+"F0.wireOp",EDGE,"E25.0"),sQuery(id+"F0.wireOp",EDGE,"E25.1"),sQuery(id+"F0.wireOp",EDGE,"E25.2"),sQuery(id+"F0.wireOp",EDGE,"E25.3"),sQuery(id+"F0.wireOp",EDGE,"E25.4"),sQuery(id+"F0.wireOp",EDGE,"E25.5"),sQuery(id+"F0.wireOp",EDGE,"E25.6"),sQuery(id+"F0.wireOp",EDGE,"E25.7")])],"isStart":false})})});
            extrude(context, id + "F14", {"entities" : qUnion([Q0]), "operationType" : NewBodyOperationType.REMOVE, "endBound" : BoundingType.UP_TO_SURFACE, "endBoundEntityFace" : qUnion([Q1]), "depth" : 25 * mm});
        }
        {
            var Q0;
            Q0=makeQuery(id+"F4.boolean.opBoolean","COPY",EDGE,{"derivedFrom":makeQuery(id+"F4.opExtrude","CAP_EDGE",EDGE,{"disambiguationData":[OSD([sQuery(id+"F0.wireOp",EDGE,"E25.6")])],"isStart":false})});
            var Q1;
            Q1=makeQuery(id+"F9.boolean.opBoolean","INTERSECT",EDGE,{"derivedFrom":[makeQuery(id+"F6.opExtrude","SWEPT_FACE",FACE,{"disambiguationData":[OSD([sQuery(id+"F5.wireOp",EDGE,"E44")])]}),makeQuery(id+"F9.opExtrude","CAP_FACE",FACE,{"disambiguationData":[OSD([sQuery(id+"F8.wireOp",EDGE,"E81")])],"isStart":false})]});
            var Q2;
            Q2=makeQuery(id+"F9.boolean.opBoolean","INTERSECT",EDGE,{"disambiguationData":[OD(1.0)],"derivedFrom":[makeQuery(id+"F6.opExtrude","SWEPT_FACE",FACE,{"disambiguationData":[OSD([sQuery(id+"F5.wireOp",EDGE,"E44")])]}),makeQuery(id+"F9.opExtrude","SWEPT_FACE",FACE,{"disambiguationData":[OSD([sQuery(id+"F8.wireOp",EDGE,"E81")])]})]});
            var Q3;
            {var subQ0=sQuery(id+"F5.wireOp",EDGE,"E44");Q3=makeQuery(id+"F9.boolean.opBoolean","SPLIT",EDGE,{"disambiguationData":[TD([makeQuery(id+"F6.opExtrude","SWEPT_FACE",FACE,{"disambiguationData":[OSD([sQuery(id+"F5.wireOp",EDGE,"E49.filletArc")])]})])],"derivedFrom":makeQuery(id+"F6.opExtrude","CAP_EDGE",EDGE,{"disambiguationData":[OSD([subQ0])],"isStart":false})});}
            var Q4;
            {var subQ0=sQuery(id+"F0.wireOp",EDGE,"E25.7");var subQ1=sQuery(id+"F0.wireOp",EDGE,"E25.6");var subQ2=sQuery(id+"F0.wireOp",EDGE,"E25.5");var subQ3=sQuery(id+"F0.wireOp",EDGE,"E25.4");var subQ4=sQuery(id+"F0.wireOp",EDGE,"E25.0");var subQ5=sQuery(id+"F0.wireOp",EDGE,"E25.1");var subQ6=sQuery(id+"F0.wireOp",EDGE,"E25.2");var subQ7=sQuery(id+"F0.wireOp",EDGE,"E25.3");Q4=makeQuery(id+"F9.boolean.opBoolean","INTERSECT",EDGE,{"derivedFrom":[makeQuery(id+"F6.boolean.opBoolean","SPLIT",FACE,{"disambiguationData":[TD([makeQuery(id+"F2.opExtrude","SWEPT_FACE",FACE,{"disambiguationData":[OSD([subQ4])]})])],"derivedFrom":makeQuery(id+"F4.boolean.opBoolean","COPY",FACE,{"derivedFrom":makeQuery(id+"F4.opExtrude","CAP_FACE",FACE,{"disambiguationData":[OSD([subQ4,subQ5,subQ6,subQ7,subQ3,subQ2,subQ1,subQ0])],"isStart":false})})}),makeQuery(id+"F9.opExtrude","SWEPT_FACE",FACE,{"disambiguationData":[OSD([sQuery(id+"F8.wireOp",EDGE,"E81")])]})]});}
            var Q5;
            Q5=makeQuery(id+"F9.boolean.opBoolean","INTERSECT",EDGE,{"disambiguationData":[OD(0.0)],"derivedFrom":[makeQuery(id+"F6.opExtrude","SWEPT_FACE",FACE,{"disambiguationData":[OSD([sQuery(id+"F5.wireOp",EDGE,"E44")])]}),makeQuery(id+"F9.opExtrude","SWEPT_FACE",FACE,{"disambiguationData":[OSD([sQuery(id+"F8.wireOp",EDGE,"E81")])]})]});
            fillet(context, id + "F15", {"entities" : qUnion([Q0, Q1, Q2, Q3, Q4, Q5]), "radius" : 3 * mm, "tangentPropagation" : true, "allowEdgeOverflow" : false});
        }
        {
            var Q0;
            Q0=makeQuery(id+"F1.opExtrude","CAP_EDGE",EDGE,{"disambiguationData":[OSD([sQuery(id+"F0.wireOp",EDGE,"E1.bottom")])],"isStart":false});
            fillet(context, id + "F16", {"entities" : qUnion([Q0]), "radius" : 2 * mm, "tangentPropagation" : true, "allowEdgeOverflow" : false});
        }
        {
            var Q0;
            Q0 = qSketchRegion(id + "F0", true);
            var Q1;
            Q1=makeQuery(id+"F2.opExtrude","CAP_FACE",FACE,{"disambiguationData":[OSD([sQuery(id+"F0.wireOp",EDGE,"E12"),sQuery(id+"F0.wireOp",EDGE,"E13"),sQuery(id+"F0.wireOp",EDGE,"E14"),sQuery(id+"F0.wireOp",EDGE,"E15"),sQuery(id+"F0.wireOp",EDGE,"E17.filletArc"),sQuery(id+"F0.wireOp",EDGE,"E18.filletArc"),sQuery(id+"F0.wireOp",EDGE,"E19.filletArc"),sQuery(id+"F0.wireOp",EDGE,"E20.filletArc"),sQuery(id+"F0.wireOp",EDGE,"E25.0"),sQuery(id+"F0.wireOp",EDGE,"E25.1"),sQuery(id+"F0.wireOp",EDGE,"E25.2"),sQuery(id+"F0.wireOp",EDGE,"E25.3"),sQuery(id+"F0.wireOp",EDGE,"E25.4"),sQuery(id+"F0.wireOp",EDGE,"E25.5"),sQuery(id+"F0.wireOp",EDGE,"E25.6"),sQuery(id+"F0.wireOp",EDGE,"E25.7")])],"isStart":false});
            extrude(context, id + "F17", {"entities" : qUnion([Q0]), "endBound" : BoundingType.UP_TO_SURFACE, "depth" : 6 * mm, "endBoundEntityFace" : qUnion([Q1]), "offsetDistance" : 25 * mm});
        }
    });
